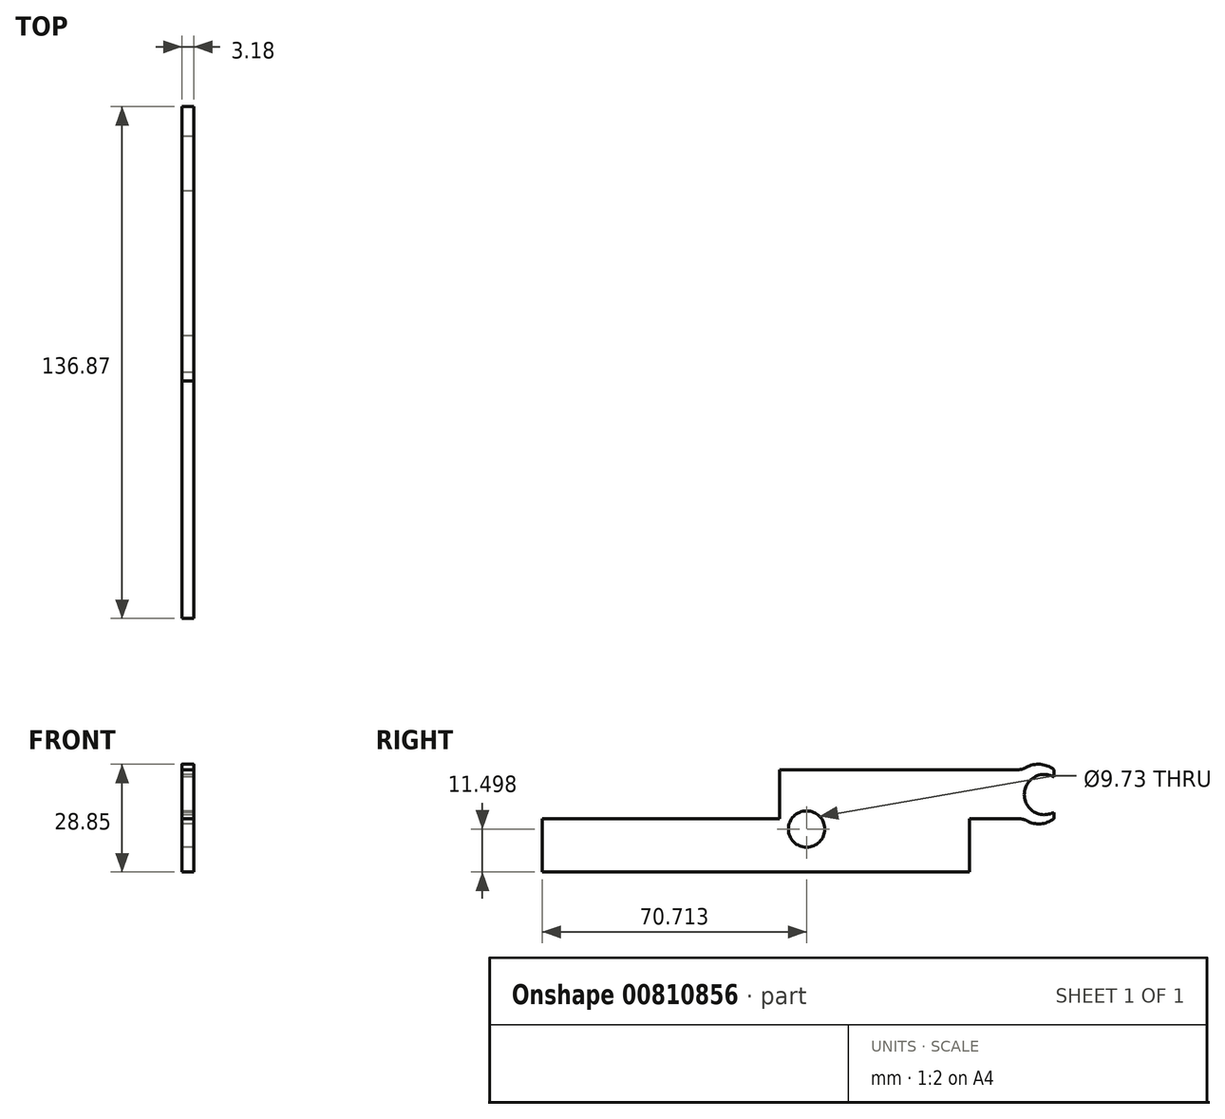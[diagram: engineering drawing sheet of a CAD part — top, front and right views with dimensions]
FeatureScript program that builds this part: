
annotation { "Feature Type Name" : "Feature", "Feature Type Description" : "" }
export const myFeature = defineFeature(function(context is Context, id is Id, definition is map)
    precondition{}
    {
        {
            var Q0;
            Q0=qCreatedBy(makeId("Right.planeOp"),FACE);
            var sketch = newSketch(context, id + "F0", { "sketchPlane" : qUnion([Q0])});
            skLineSegment(sketch, "E0.bottom", {"start": v(57.15, 7.14) * mm, "end": v(-57.15, 7.14) * mm});
            skLineSegment(sketch, "E0.top", {"start": v(57.15, -7.14) * mm, "end": v(-57.15, -7.14) * mm});
            skLineSegment(sketch, "E0.left", {"start": v(57.15, 7.14) * mm, "end": v(57.15, -7.14) * mm});
            skLineSegment(sketch, "E0.right", {"start": v(-57.15, 7.14) * mm, "end": v(-57.15, -7.14) * mm});
            skPoint(sketch, "E0.middle", {"position": v(0, 0) * mm});
            skCircle(sketch, "E1", {"center": v(13.56, 4.36) * mm, "radius": 4.87 * mm});
            skLineSegment(sketch, "E2.bottom", {"start": v(57.15, 7.14) * mm, "end": v(0, 7.14) * mm});
            skLineSegment(sketch, "E2.left", {"start": v(57.15, 7.14) * mm, "end": v(57.15, 7.14) * mm});
            skLineSegment(sketch, "E2.right", {"start": v(0, 7.14) * mm, "end": v(0, 7.14) * mm});
            skLineSegment(sketch, "E3.top", {"start": v(0, 7.14) * mm, "end": v(57.15, 7.14) * mm});
            skLineSegment(sketch, "E3.right", {"start": v(57.15, 20.25) * mm, "end": v(57.15, 7.14) * mm});
            skLineSegment(sketch, "E4.bottom", {"start": v(57.15, 20.25) * mm, "end": v(70.08, 20.25) * mm});
            skLineSegment(sketch, "E4.top", {"start": v(57.15, 7.14) * mm, "end": v(70.31, 7.14) * mm});
            skLineSegment(sketch, "E4.right", {"start": v(79.72, 20.25) * mm, "end": v(79.72, 7.14) * mm});
            skArc(sketch, "E5", {"start": v(79.72, 18.36) * mm, "mid": v(71.8, 13.6) * mm, "end": v(79.72, 8.83) * mm});
            skLineSegment(sketch, "E6.bottom", {"start": v(57.15, 7.14) * mm, "end": v(6.35, 7.14) * mm});
            skLineSegment(sketch, "E6.top", {"start": v(57.15, 20.25) * mm, "end": v(6.35, 20.25) * mm});
            skLineSegment(sketch, "E6.left", {"start": v(57.15, 7.14) * mm, "end": v(57.15, 20.25) * mm});
            skLineSegment(sketch, "E6.right", {"start": v(6.35, 7.14) * mm, "end": v(6.35, 20.25) * mm});
            skArc(sketch, "E7", {"start": v(79.72, 20.25) * mm, "mid": v(76.1, 21.7) * mm, "end": v(72.28, 20.84) * mm});
            skArc(sketch, "E8", {"start": v(72.46, 6.59) * mm, "mid": v(76.17, 5.78) * mm, "end": v(79.72, 7.14) * mm});
            skPoint(sketch, "E9.newPointA", {"position": v(71.35, 20.19) * mm});
            skPoint(sketch, "E9.newPointB", {"position": v(79.72, 20.25) * mm});
            skArc(sketch, "E9.filletArc", {"start": v(70.08, 20.25) * mm, "mid": v(71.22, 20.4) * mm, "end": v(72.28, 20.84) * mm});
            skPoint(sketch, "E10.newPointA", {"position": v(71.35, 7.36) * mm});
            skPoint(sketch, "E10.newPointB", {"position": v(79.72, 7.14) * mm});
            skArc(sketch, "E10.filletArc", {"start": v(72.46, 6.59) * mm, "mid": v(71.42, 7) * mm, "end": v(70.31, 7.14) * mm});
            skSolve(sketch);
        }
        {
            var Q0;
            Q0=makeQuery(id+"F0.imprint","IMPRINT",FACE,{"disambiguationData":[TD([[makeQuery(id+"F0.imprint","IMPRINT",EDGE,{"derivedFrom":sQuery(id+"F0.wireOp",EDGE,"E6.top")}),1.0]])]});
            var Q1;
            Q1=makeQuery(id+"F0.imprint","IMPRINT",FACE,{"disambiguationData":[TD([[makeQuery(id+"F0.imprint","IMPRINT",EDGE,{"derivedFrom":sQuery(id+"F0.wireOp",EDGE,"E0.bottom")}),1.0]])]});
            var Q2;
            Q2=makeQuery(id+"F0.imprint","IMPRINT",FACE,{"disambiguationData":[TD([[makeQuery(id+"F0.imprint","IMPRINT",EDGE,{"derivedFrom":sQuery(id+"F0.wireOp",EDGE,"E4.bottom")}),-1.0]])]});
            extrude(context, id + "F1", {"entities" : qUnion([Q0, Q1, Q2]), "depth" : 3.17 * mm, "offsetDistance" : 25.4 * mm});
        }
    });
